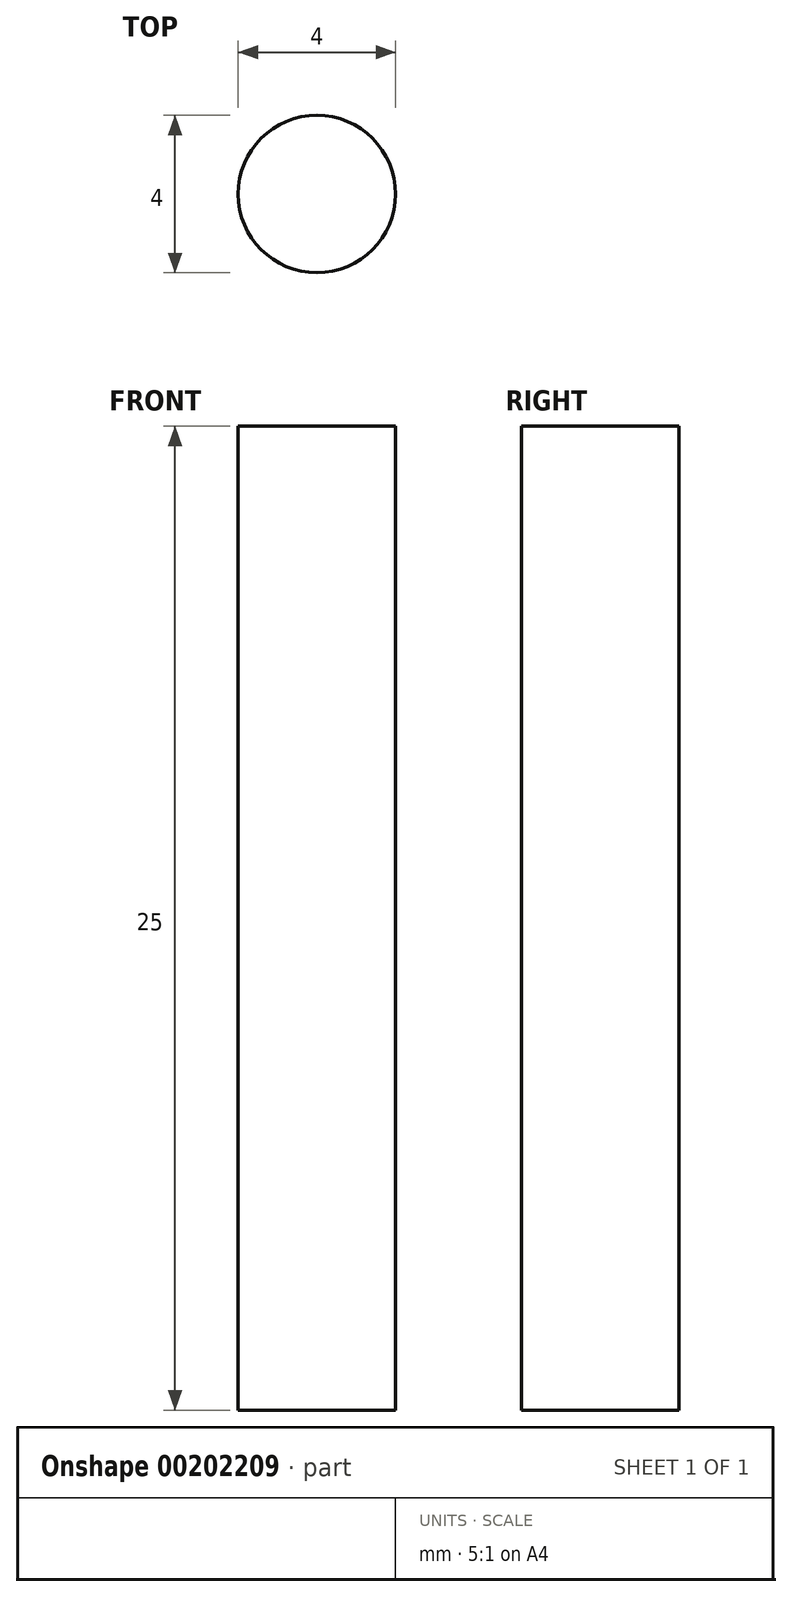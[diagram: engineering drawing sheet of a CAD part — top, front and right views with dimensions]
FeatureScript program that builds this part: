
annotation { "Feature Type Name" : "Feature", "Feature Type Description" : "" }
export const myFeature = defineFeature(function(context is Context, id is Id, definition is map)
    precondition{}
    {
        {
            var Q0;
            Q0=qCreatedBy(makeId("Top.planeOp"),FACE);
            var sketch = newSketch(context, id + "F0", { "sketchPlane" : qUnion([Q0])});
            skCircle(sketch, "E0", {"center": v(0, 0) * mm, "radius": 2 * mm});
            skSolve(sketch);
        }
        {
            var Q0;
            Q0 = qSketchRegion(id + "F0", true);
            extrude(context, id + "F1", {"entities" : qUnion([Q0]), "depth" : 25 * mm});
        }
    });
